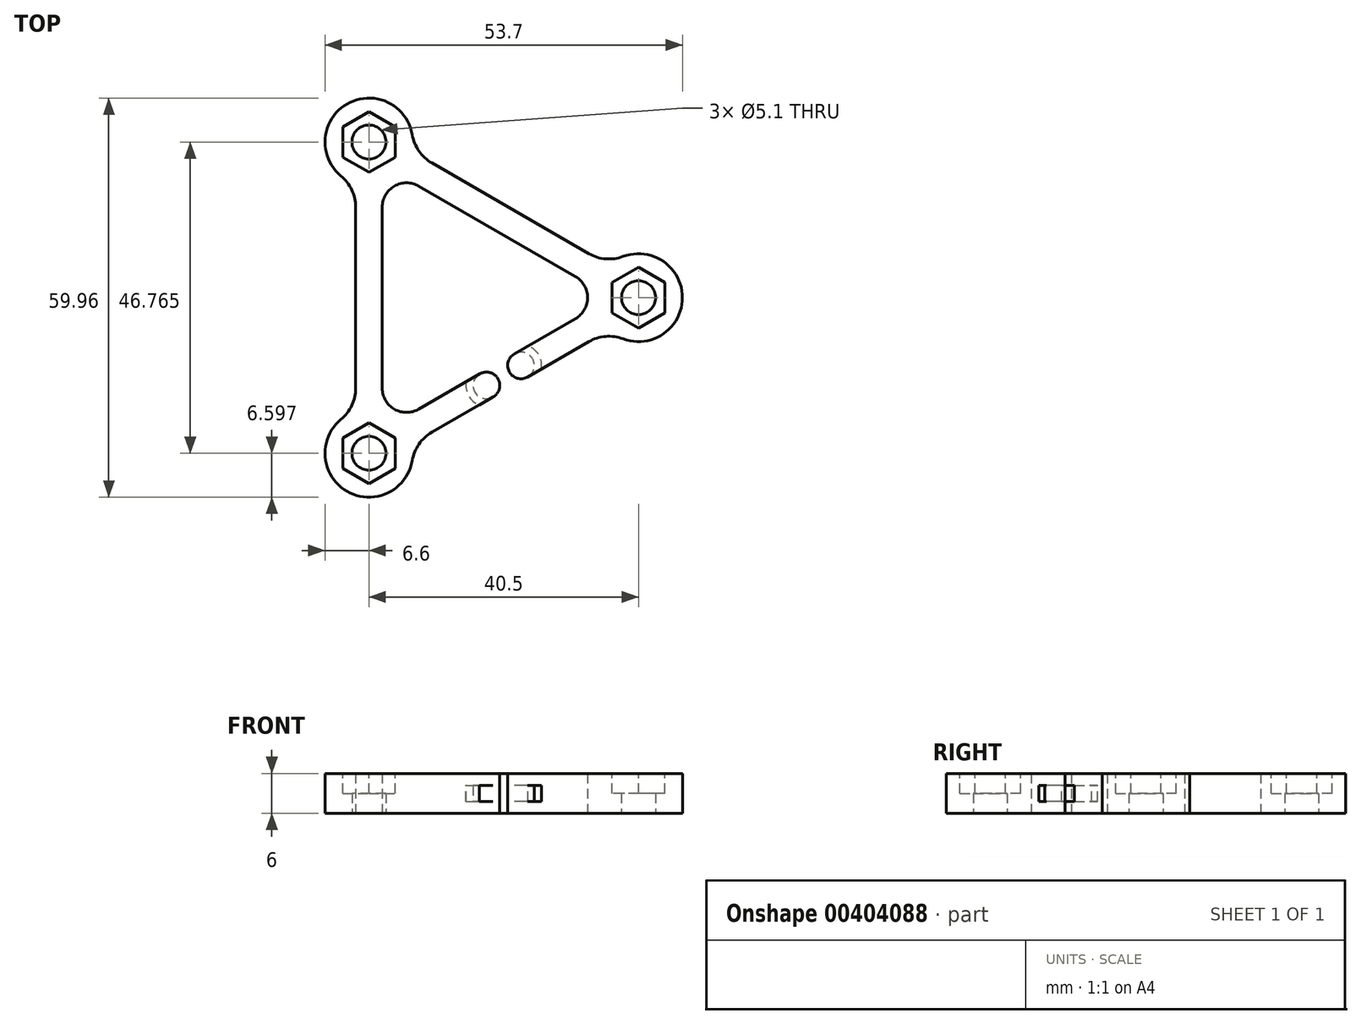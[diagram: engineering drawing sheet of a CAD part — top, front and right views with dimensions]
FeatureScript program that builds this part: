
annotation { "Feature Type Name" : "Feature", "Feature Type Description" : "" }
export const myFeature = defineFeature(function(context is Context, id is Id, definition is map)
    precondition{}
    {
        {
            var Q0;
            Q0=qCreatedBy(makeId("Top.planeOp"),FACE);
            var sketch = newSketch(context, id + "F0", { "sketchPlane" : qUnion([Q0])});
            skCircle(sketch, "E0", {"center": v(-40.5, 23.38) * mm, "radius": 2.55 * mm});
            skCircle(sketch, "E1", {"center": v(-40.5, -23.38) * mm, "radius": 2.55 * mm});
            skCircle(sketch, "E2", {"center": v(0, 0) * mm, "radius": 2.55 * mm});
            skArc(sketch, "E3", {"start": v(-34, 24.49) * mm, "mid": v(-43.8, 29.1) * mm, "end": v(-44.7, 18.3) * mm});
            skArc(sketch, "E4", {"start": v(-44.7, -18.3) * mm, "mid": v(-43.8, -29.1) * mm, "end": v(-34, -24.49) * mm});
            skArc(sketch, "E5", {"start": v(-2.3, -6.19) * mm, "mid": v(6.6, 0) * mm, "end": v(-2.3, 6.19) * mm});
            skLineSegment(sketch, "E6", {"start": v(-33.03, 16.76) * mm, "end": v(-9.47, 3.16) * mm});
            skLineSegment(sketch, "E7", {"start": v(-31.03, 20.22) * mm, "end": v(-7.47, 6.62) * mm});
            skLineSegment(sketch, "E8", {"start": v(-40.5, 23.38) * mm, "end": v(0, 0) * mm, "construction": true});
            skLineSegment(sketch, "E9", {"start": v(0, 0) * mm, "end": v(-40.5, -23.38) * mm, "construction": true});
            skLineSegment(sketch, "E10", {"start": v(-40.5, -23.38) * mm, "end": v(-40.5, 23.38) * mm, "construction": true});
            skArc(sketch, "E11", {"start": v(-33.03, 16.76) * mm, "mid": v(-36.68, 16.76) * mm, "end": v(-38.5, 13.6) * mm});
            skArc(sketch, "E12", {"start": v(-38.5, -13.6) * mm, "mid": v(-36.68, -16.76) * mm, "end": v(-33.03, -16.76) * mm});
            skArc(sketch, "E13", {"start": v(-9.47, -3.16) * mm, "mid": v(-7.65, 0) * mm, "end": v(-9.47, 3.16) * mm});
            skArc(sketch, "E14", {"start": v(-44.7, -18.3) * mm, "mid": v(-43.08, -16.2) * mm, "end": v(-42.5, -13.6) * mm});
            skArc(sketch, "E15", {"start": v(-31.03, -20.22) * mm, "mid": v(-32.99, -22.02) * mm, "end": v(-34, -24.49) * mm});
            skArc(sketch, "E16", {"start": v(-42.5, 13.6) * mm, "mid": v(-43.08, 16.2) * mm, "end": v(-44.7, 18.3) * mm});
            skArc(sketch, "E17", {"start": v(-34, 24.49) * mm, "mid": v(-32.99, 22.02) * mm, "end": v(-31.03, 20.22) * mm});
            skArc(sketch, "E18", {"start": v(-7.47, 6.62) * mm, "mid": v(-4.93, 5.83) * mm, "end": v(-2.3, 6.19) * mm});
            skArc(sketch, "E19", {"start": v(-2.3, -6.19) * mm, "mid": v(-4.93, -5.83) * mm, "end": v(-7.47, -6.62) * mm});
            skLineSegment(sketch, "E20", {"start": v(-33.03, 16.76) * mm, "end": v(-31.03, 20.22) * mm, "construction": true});
            skLineSegment(sketch, "E21", {"start": v(-9.47, 3.16) * mm, "end": v(-7.47, 6.62) * mm, "construction": true});
            skLineSegment(sketch, "E22", {"start": v(-9.47, -3.16) * mm, "end": v(-7.47, -6.62) * mm, "construction": true});
            skLineSegment(sketch, "E23", {"start": v(-42.5, -13.6) * mm, "end": v(-38.5, -13.6) * mm, "construction": true});
            skLineSegment(sketch, "E24", {"start": v(-31.03, -20.22) * mm, "end": v(-33.03, -16.76) * mm, "construction": true});
            skLineSegment(sketch, "E25", {"start": v(-42.5, -13.6) * mm, "end": v(-42.5, 13.6) * mm});
            skLineSegment(sketch, "E26", {"start": v(-38.5, -13.6) * mm, "end": v(-38.5, 13.6) * mm});
            skLineSegment(sketch, "E27", {"start": v(-42.5, 13.6) * mm, "end": v(-38.5, 13.6) * mm, "construction": true});
            skLineSegment(sketch, "E28", {"start": v(-33.03, -16.76) * mm, "end": v(-23.85, -11.46) * mm});
            skLineSegment(sketch, "E29", {"start": v(-18.65, -8.46) * mm, "end": v(-9.47, -3.16) * mm});
            skLineSegment(sketch, "E30", {"start": v(-31.03, -20.22) * mm, "end": v(-21.85, -14.92) * mm});
            skLineSegment(sketch, "E31", {"start": v(-7.47, -6.62) * mm, "end": v(-16.65, -11.92) * mm});
            skArc(sketch, "E32", {"start": v(-21.85, -14.92) * mm, "mid": v(-21.12, -12.2) * mm, "end": v(-23.85, -11.46) * mm});
            skArc(sketch, "E33", {"start": v(-18.65, -8.46) * mm, "mid": v(-19.38, -11.2) * mm, "end": v(-16.65, -11.92) * mm});
            skSolve(sketch);
        }
        {
            var Q0;
            Q0=makeQuery(id+"F0.imprint","IMPRINT",FACE,{"disambiguationData":[TD([[makeQuery(id+"F0.imprint","IMPRINT",EDGE,{"derivedFrom":sQuery(id+"F0.wireOp",EDGE,"E0")}),-1.0]])]});
            extrude(context, id + "F1", {"entities" : qUnion([Q0]), "depth" : 6 * mm});
        }
        {
            var Q0;
            Q0=makeQuery(id+"F1.opExtrude","CAP_FACE",FACE,{"disambiguationData":[OSD([sQuery(id+"F0.wireOp",EDGE,"E0"),sQuery(id+"F0.wireOp",EDGE,"E1"),sQuery(id+"F0.wireOp",EDGE,"E2"),sQuery(id+"F0.wireOp",EDGE,"E3"),sQuery(id+"F0.wireOp",EDGE,"E4"),sQuery(id+"F0.wireOp",EDGE,"E5"),sQuery(id+"F0.wireOp",EDGE,"T5Vw66OG-G5OR-DHDx-KvU7-dnTMRq0o1A0g"),sQuery(id+"F0.wireOp",EDGE,"8mzCXc7P-Lu7A-tcA2-hDls-zUZMRrlwUirj"),sQuery(id+"F0.wireOp",EDGE,"n4Ubmgs8-MzYA-ilAs-um63-DOsCIZ42xYd5"),sQuery(id+"F0.wireOp",EDGE,"iCspHw3C-Pdpp-QPBW-yDHl-MGOv44Ga2VXa"),sQuery(id+"F0.wireOp",EDGE,"xnWTmErK-ZSIG-ryMW-Ekzr-RR3PqCajZfuL"),sQuery(id+"F0.wireOp",EDGE,"AKW5OVUo-PFRE-jSi0-v7oE-Iw4JobIG5vWv"),sQuery(id+"F0.wireOp",EDGE,"E6"),sQuery(id+"F0.wireOp",EDGE,"JkiSf5jC-OJZR-1wmq-AVkU-QwjWYPwXVpW3"),sQuery(id+"F0.wireOp",EDGE,"9YlTFYq7-sXvY-dmJ4-6YRE-gBgDyT6P94yA")])],"isStart":false});
            var sketch = newSketch(context, id + "F2", { "sketchPlane" : qUnion([Q0])});
            skCircle(sketch, "E34.cCircle", {"center": v(-40.5, 23.38) * mm, "radius": 3.95 * mm, "construction": true});
            skLineSegment(sketch, "E34.0", {"start": v(-36.55, 25.66) * mm, "end": v(-36.55, 21.1) * mm});
            skLineSegment(sketch, "E34.1", {"start": v(-36.55, 21.1) * mm, "end": v(-40.5, 18.82) * mm});
            skLineSegment(sketch, "E34.2", {"start": v(-40.5, 18.82) * mm, "end": v(-44.45, 21.1) * mm});
            skLineSegment(sketch, "E34.3", {"start": v(-44.45, 21.1) * mm, "end": v(-44.45, 25.66) * mm});
            skLineSegment(sketch, "E34.4", {"start": v(-44.45, 25.66) * mm, "end": v(-40.5, 27.94) * mm});
            skLineSegment(sketch, "E34.5", {"start": v(-40.5, 27.94) * mm, "end": v(-36.55, 25.66) * mm});
            skPoint(sketch, "E34.0.midPoint", {"position": v(-36.55, 23.38) * mm});
            skCircle(sketch, "E35.cCircle", {"center": v(-40.5, -23.38) * mm, "radius": 3.95 * mm, "construction": true});
            skLineSegment(sketch, "E35.0", {"start": v(-36.55, -21.1) * mm, "end": v(-36.55, -25.66) * mm});
            skLineSegment(sketch, "E35.1", {"start": v(-36.55, -25.66) * mm, "end": v(-40.5, -27.94) * mm});
            skLineSegment(sketch, "E35.2", {"start": v(-40.5, -27.94) * mm, "end": v(-44.45, -25.66) * mm});
            skLineSegment(sketch, "E35.3", {"start": v(-44.45, -25.66) * mm, "end": v(-44.45, -21.1) * mm});
            skLineSegment(sketch, "E35.4", {"start": v(-44.45, -21.1) * mm, "end": v(-40.5, -18.82) * mm});
            skLineSegment(sketch, "E35.5", {"start": v(-40.5, -18.82) * mm, "end": v(-36.55, -21.1) * mm});
            skPoint(sketch, "E35.0.midPoint", {"position": v(-36.55, -23.38) * mm});
            skCircle(sketch, "E36.cCircle", {"center": v(0, 0) * mm, "radius": 3.95 * mm, "construction": true});
            skLineSegment(sketch, "E36.0", {"start": v(-3.95, -2.28) * mm, "end": v(-3.95, 2.28) * mm});
            skLineSegment(sketch, "E36.1", {"start": v(-3.95, 2.28) * mm, "end": v(0, 4.56) * mm});
            skLineSegment(sketch, "E36.2", {"start": v(0, 4.56) * mm, "end": v(3.95, 2.28) * mm});
            skLineSegment(sketch, "E36.3", {"start": v(3.95, 2.28) * mm, "end": v(3.95, -2.28) * mm});
            skLineSegment(sketch, "E36.4", {"start": v(3.95, -2.28) * mm, "end": v(0, -4.56) * mm});
            skLineSegment(sketch, "E36.5", {"start": v(0, -4.56) * mm, "end": v(-3.95, -2.28) * mm});
            skPoint(sketch, "E36.0.midPoint", {"position": v(-3.95, 0) * mm});
            skLineSegment(sketch, "E37", {"start": v(-40.5, -23.38) * mm, "end": v(-27, 0) * mm, "construction": true});
            skLineSegment(sketch, "E38", {"start": v(-27, 0) * mm, "end": v(-40.5, 23.38) * mm, "construction": true});
            skLineSegment(sketch, "E39", {"start": v(-27, 0) * mm, "end": v(0, 0) * mm, "construction": true});
            skLineSegment(sketch, "E40", {"start": v(-35, 0) * mm, "end": v(-23, 6.93) * mm, "construction": true});
            skPoint(sketch, "E40.startSnap0", {"position": v(-13.5, 0) * mm});
            skLineSegment(sketch, "E41", {"start": v(-23, 6.93) * mm, "end": v(-23, -6.93) * mm, "construction": true});
            skLineSegment(sketch, "E42", {"start": v(-23, -6.93) * mm, "end": v(-35, 0) * mm, "construction": true});
            skPoint(sketch, "E43", {"position": v(-29, 3.46) * mm});
            skPoint(sketch, "E44", {"position": v(-29, -3.46) * mm});
            skPoint(sketch, "E45", {"position": v(-23, 0) * mm});
            skSolve(sketch);
        }
        {
            var Q0;
            Q0=qSketchRegion(id+"F2",true);
            extrude(context, id + "F3", {"entities" : qUnion([Q0]), "operationType" : NewBodyOperationType.REMOVE, "oppositeDirection" : true, "depth" : 3 * mm});
        }
        {
            var Q0;
            Q0=qCreatedBy(makeId("Top.planeOp"),FACE);
            var Q1;
            Q1=makeQuery(id+"F2.imprint","IMPRINT",FACE,{"disambiguationData":[TD([[makeQuery(id+"F2.imprint","IMPRINT",EDGE,{"derivedFrom":sQuery(id+"F2.wireOp",EDGE,"E34.0")}),1.0]])]});
            cPlane(context, id + "F4", {"entities" : qUnion([Q0, Q1]), "cplaneType" : CPlaneType.MID_PLANE, "offset" : 3 * mm, "oppositeDirection" : true, "width" : 150 * mm, "height" : 150 * mm});
        }
        {
            var Q0;
            Q0=qCreatedBy(id+"F4.planeOp",FACE);
            var sketch = newSketch(context, id + "F5", { "sketchPlane" : qUnion([Q0])});
            skLineSegment(sketch, "E46", {"start": v(-21.85, -14.92) * mm, "end": v(-21.85, -14.92) * mm});
            skLineSegment(sketch, "E47", {"start": v(-23.85, -11.46) * mm, "end": v(-23.85, -11.46) * mm});
            skLineSegment(sketch, "E48", {"start": v(-16.65, -11.92) * mm, "end": v(-16.65, -11.92) * mm});
            skLineSegment(sketch, "E49", {"start": v(-18.65, -8.46) * mm, "end": v(-18.65, -8.46) * mm});
            skArc(sketch, "E50", {"start": v(-25.9, -12.64) * mm, "mid": v(-25.53, -14.74) * mm, "end": v(-23.9, -16.1) * mm});
            skArc(sketch, "E51", {"start": v(-16.65, -11.92) * mm, "mid": v(-15.92, -9.2) * mm, "end": v(-18.65, -8.46) * mm});
            skArc(sketch, "E52", {"start": v(-23.85, -11.46) * mm, "mid": v(-24.58, -14.2) * mm, "end": v(-21.85, -14.92) * mm});
            skLineSegment(sketch, "E53", {"start": v(-25.9, -12.64) * mm, "end": v(-23.85, -11.46) * mm});
            skLineSegment(sketch, "E54", {"start": v(-21.85, -14.92) * mm, "end": v(-23.9, -16.1) * mm});
            skArc(sketch, "E55", {"start": v(-14.6, -10.74) * mm, "mid": v(-14.97, -8.64) * mm, "end": v(-16.6, -7.28) * mm});
            skLineSegment(sketch, "E56", {"start": v(-16.6, -7.28) * mm, "end": v(-18.65, -8.46) * mm});
            skLineSegment(sketch, "E57", {"start": v(-16.65, -11.92) * mm, "end": v(-14.6, -10.74) * mm});
            skSolve(sketch);
        }
        {
            var Q0;
            Q0=qSketchRegion(id+"F5",true);
            extrude(context, id + "F6", {"entities" : qUnion([Q0]), "operationType" : NewBodyOperationType.REMOVE, "endBound" : BoundingType.SYMMETRIC, "oppositeDirection" : true, "depth" : 2.4 * mm});
        }
    });
